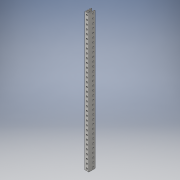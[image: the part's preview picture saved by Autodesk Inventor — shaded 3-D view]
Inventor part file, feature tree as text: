
AUTODESK INVENTOR PART (.ipt)
format: ipt  version: 2016 (Build 200138000, 138)  size: 249,856 bytes
history: native  units: in
note: dims shown in document units (in); Inventor stores cm internally (conversion verified against a paired STEP export)
features: fillet x1
ambient origin geometry x8: Origin, YZ Plane, XZ Plane, XY Plane, X Axis, Y Axis, Z Axis, Center Point
bodies: Solid1 (feature_tree)
feature tree (1):
  fillet  "Fillet1"  [1 undecoded]
note: 1 required parameter value undecoded (feature->parameter linkage not recoverable at this tier; creation-order binding heuristic only, values carry confidence <= 0.55)
